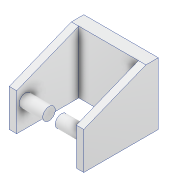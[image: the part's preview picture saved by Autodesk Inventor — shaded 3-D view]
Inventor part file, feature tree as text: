
AUTODESK INVENTOR PART (.ipt)
format: ipt  version: 2020 (Build 240168000, 168)  size: 175,616 bytes
history: native  units: mm
features: extrude x8, sketch x8, projected_geometry x3, other x1
ambient origin geometry x8: Origin, YZ Plane, XZ Plane, XY Plane, X Axis, Y Axis, Z Axis, Center Point
bodies: Body1 (feature_tree)
feature tree (20):
  other  "솔리드1"
  extrude  "돌출1"  Depth=30.0mm
  extrude  "돌출2"  Depth=30.0mm
  extrude  "돌출3"  Depth=5.0mm TaperAngle=0.0deg
  extrude  "돌출4"  Depth=3.0mm
  extrude  "돌출5"  Depth=3.0mm
  extrude  "돌출6"  Depth=30.0mm TaperAngle=0.0deg
  extrude  "돌출7"  Depth=10.0mm
  extrude  "돌출8"  Depth=5.0mm TaperAngle=0.0deg
  sketch  "스케치1"
  sketch  "스케치2"
  sketch  "스케치3"
  sketch  "스케치4"
  sketch  "스케치5"
  sketch  "스케치6"
  projected_geometry  "투영된 루프1"
  projected_geometry  "투영된 루프2"
  sketch  "스케치7"
  projected_geometry  "투영된 루프3"
  sketch  "스케치8"
